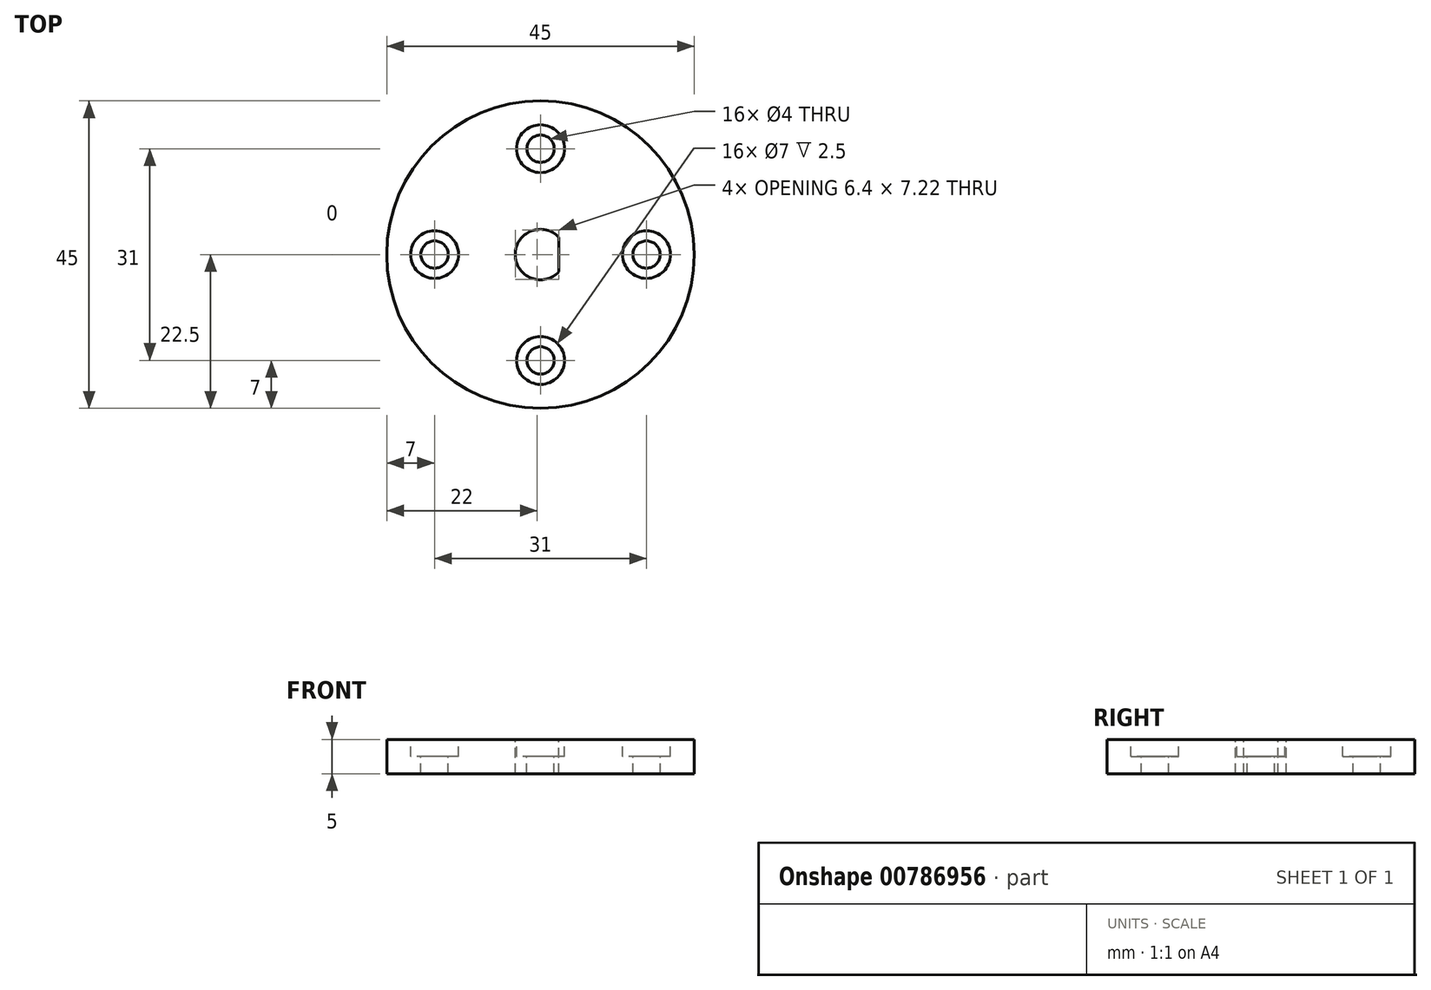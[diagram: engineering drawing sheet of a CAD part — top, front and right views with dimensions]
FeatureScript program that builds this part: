
annotation { "Feature Type Name" : "Feature", "Feature Type Description" : "" }
export const myFeature = defineFeature(function(context is Context, id is Id, definition is map)
    precondition{}
    {
        {
            var Q0;
            Q0=qCreatedBy(makeId("Top.planeOp"),FACE);
            var sketch = newSketch(context, id + "F0", { "sketchPlane" : qUnion([Q0])});
            skCircle(sketch, "E0", {"center": v(0, 0) * mm, "radius": 22.5 * mm});
            skSolve(sketch);
        }
        {
            var Q0;
            Q0 = qSketchRegion(id + "F0", true);
            extrude(context, id + "F1", {"entities" : qUnion([Q0]), "depth" : 5 * mm, "offsetDistance" : 25 * mm});
        }
        {
            var Q0;
            Q0=makeQuery(id+"F1.opExtrude","CAP_FACE",FACE,{"disambiguationData":[OSD([sQuery(id+"F0.wireOp",EDGE,"E0")])],"isStart":false});
            var sketch = newSketch(context, id + "F2", { "sketchPlane" : qUnion([Q0])});
            skCircle(sketch, "E1", {"center": v(0, 0) * mm, "radius": 3.7 * mm});
            skLineSegment(sketch, "E2", {"start": v(0, 0) * mm, "end": v(2.7, 0) * mm});
            skLineSegment(sketch, "E3", {"start": v(2.7, 0) * mm, "end": v(2.7, 2.53) * mm});
            skLineSegment(sketch, "E4", {"start": v(2.7, 2.53) * mm, "end": v(2.7, -2.53) * mm});
            skSolve(sketch);
        }
        {
            var Q0;
            {var subQ0=sQuery(id+"F2.wireOp",EDGE,"E4");var subQ4=makeQuery(id+"F2.imprint","IMPRINT",VERTEX,{"derivedFrom":subQ0});Q0=makeQuery(id+"F2.imprint","IMPRINT",FACE,{"disambiguationData":[TD([[makeQuery(id+"F2.imprint","IMPRINT",EDGE,{"disambiguationData":[TD([[subQ4,1.0]])],"derivedFrom":subQ0}),-1.0]])]});}
            extrude(context, id + "F3", {"entities" : qUnion([Q0]), "operationType" : NewBodyOperationType.REMOVE, "oppositeDirection" : true, "depth" : 25 * mm, "offsetDistance" : 25 * mm});
        }
        {
            var Q0;
            Q0=makeQuery(id+"F1.opExtrude","CAP_FACE",FACE,{"disambiguationData":[OSD([sQuery(id+"F0.wireOp",EDGE,"E0")])],"isStart":false});
            var sketch = newSketch(context, id + "F4", { "sketchPlane" : qUnion([Q0])});
            skLineSegment(sketch, "E5", {"start": v(0, 22.5) * mm, "end": v(0, 15.5) * mm});
            skCircle(sketch, "E6", {"center": v(0, 15.5) * mm, "radius": 2 * mm});
            skSolve(sketch);
        }
        {
            var Q0;
            Q0 = qSketchRegion(id + "F4", true);
            extrude(context, id + "F5", {"entities" : qUnion([Q0]), "operationType" : NewBodyOperationType.REMOVE, "oppositeDirection" : true, "depth" : 25 * mm, "offsetDistance" : 25 * mm});
        }
        {
            var Q0;
            Q0=makeQuery(id+"F1.opExtrude","CAP_FACE",FACE,{"disambiguationData":[OSD([sQuery(id+"F0.wireOp",EDGE,"E0")])],"isStart":false});
            var sketch = newSketch(context, id + "F6", { "sketchPlane" : qUnion([Q0])});
            skLineSegment(sketch, "E7", {"start": v(22.5, 0) * mm, "end": v(15.5, 0) * mm});
            skPoint(sketch, "E7.startSnap0", {"position": v(2.7, 0) * mm});
            skCircle(sketch, "E8", {"center": v(15.5, 0) * mm, "radius": 2 * mm});
            skLineSegment(sketch, "E9", {"start": v(0, -22.5) * mm, "end": v(0, -15.5) * mm});
            skCircle(sketch, "E10", {"center": v(0, -15.5) * mm, "radius": 2 * mm});
            skLineSegment(sketch, "E11", {"start": v(-22.5, 0) * mm, "end": v(-15.5, 0) * mm});
            skCircle(sketch, "E12", {"center": v(-15.5, 0) * mm, "radius": 2 * mm});
            skSolve(sketch);
        }
        {
            var Q0;
            Q0 = qSketchRegion(id + "F6", true);
            extrude(context, id + "F7", {"entities" : qUnion([Q0]), "operationType" : NewBodyOperationType.REMOVE, "oppositeDirection" : true, "depth" : 25 * mm, "offsetDistance" : 25 * mm});
        }
        {
            var Q0;
            Q0=makeQuery(id+"F1.opExtrude","CAP_FACE",FACE,{"disambiguationData":[OSD([sQuery(id+"F0.wireOp",EDGE,"E0")])],"isStart":false});
            var sketch = newSketch(context, id + "F8", { "sketchPlane" : qUnion([Q0])});
            skCircle(sketch, "E13", {"center": v(-15.5, 0) * mm, "radius": 3.5 * mm});
            skCircle(sketch, "E14", {"center": v(15.5, 0) * mm, "radius": 3.5 * mm});
            skCircle(sketch, "E15", {"center": v(0, -15.5) * mm, "radius": 3.5 * mm});
            skCircle(sketch, "E16", {"center": v(0, 15.5) * mm, "radius": 3.5 * mm});
            skSolve(sketch);
        }
        {
            var Q0;
            Q0 = qSketchRegion(id + "F8", true);
            extrude(context, id + "F9", {"entities" : qUnion([Q0]), "operationType" : NewBodyOperationType.REMOVE, "oppositeDirection" : true, "depth" : 2.5 * mm, "offsetDistance" : 25 * mm});
        }
    });
